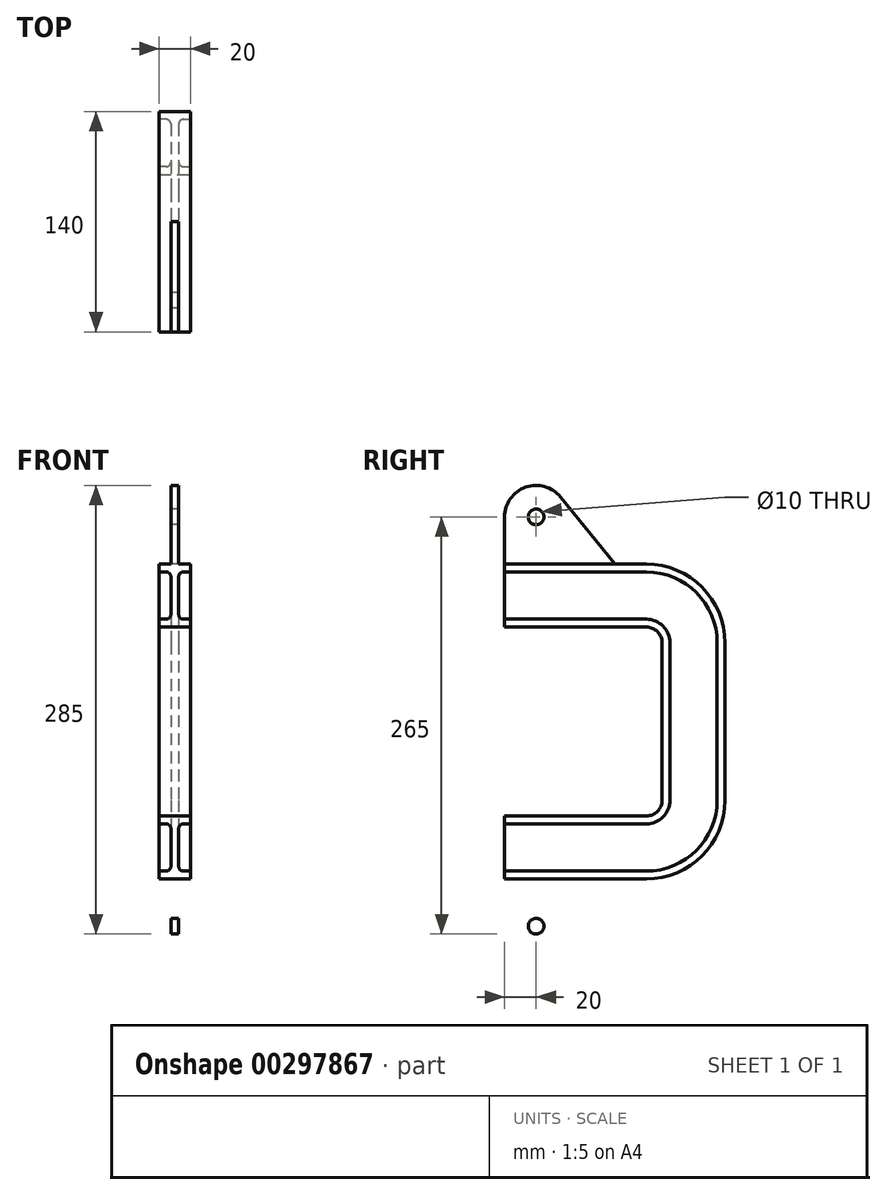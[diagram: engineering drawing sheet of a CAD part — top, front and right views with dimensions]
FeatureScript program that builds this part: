
annotation { "Feature Type Name" : "Feature", "Feature Type Description" : "" }
export const myFeature = defineFeature(function(context is Context, id is Id, definition is map)
    precondition{}
    {
        {
            var Q0;
            Q0=qCreatedBy(makeId("Front.planeOp"),FACE);
            var sketch = newSketch(context, id + "F0", { "sketchPlane" : qUnion([Q0])});
            skLineSegment(sketch, "E0", {"start": v(2.5, 0) * mm, "end": v(2.5, 12) * mm});
            skLineSegment(sketch, "E1", {"start": v(5.5, 15) * mm, "end": v(10, 15) * mm});
            skLineSegment(sketch, "E2", {"start": v(10, 15) * mm, "end": v(10, 20) * mm});
            skLineSegment(sketch, "E3", {"start": v(10, 20) * mm, "end": v(0, 20) * mm});
            skLineSegment(sketch, "E4.MirrorCS", {"start": v(-10, 15) * mm, "end": v(-10, 20) * mm});
            skLineSegment(sketch, "E5.MirrorCS", {"start": v(-5.5, 15) * mm, "end": v(-10, 15) * mm});
            skLineSegment(sketch, "E6.MirrorCS", {"start": v(-2.5, 0) * mm, "end": v(-2.5, 12) * mm});
            skLineSegment(sketch, "E7.MirrorCS", {"start": v(-10, 20) * mm, "end": v(0, 20) * mm});
            skLineSegment(sketch, "E8.MirrorCS", {"start": v(5.5, -15) * mm, "end": v(10, -15) * mm});
            skLineSegment(sketch, "E9.MirrorCS", {"start": v(-10, -15) * mm, "end": v(-10, -20) * mm});
            skLineSegment(sketch, "E10.MirrorCS", {"start": v(-5.5, -15) * mm, "end": v(-10, -15) * mm});
            skLineSegment(sketch, "E11.MirrorCS", {"start": v(10, -15) * mm, "end": v(10, -20) * mm});
            skLineSegment(sketch, "E12.MirrorCS", {"start": v(-10, -20) * mm, "end": v(0, -20) * mm});
            skLineSegment(sketch, "E13.MirrorCS", {"start": v(-2.5, 0) * mm, "end": v(-2.5, -12) * mm});
            skLineSegment(sketch, "E14.MirrorCS", {"start": v(10, -20) * mm, "end": v(0, -20) * mm});
            skLineSegment(sketch, "E15.MirrorCS", {"start": v(2.5, 0) * mm, "end": v(2.5, -12) * mm});
            skPoint(sketch, "E16.visualSharp", {"position": v(2.5, 15) * mm});
            skArc(sketch, "E16.filletArc", {"start": v(5.5, 15) * mm, "mid": v(3.38, 14.12) * mm, "end": v(2.5, 12) * mm});
            skPoint(sketch, "E17.visualSharp", {"position": v(-2.5, 15) * mm});
            skArc(sketch, "E17.filletArc", {"start": v(-2.5, 12) * mm, "mid": v(-3.38, 14.12) * mm, "end": v(-5.5, 15) * mm});
            skPoint(sketch, "E18.visualSharp", {"position": v(-2.5, -15) * mm});
            skArc(sketch, "E18.filletArc", {"start": v(-5.5, -15) * mm, "mid": v(-3.38, -14.12) * mm, "end": v(-2.5, -12) * mm});
            skPoint(sketch, "E19.visualSharp", {"position": v(2.5, -15) * mm});
            skArc(sketch, "E19.filletArc", {"start": v(2.5, -12) * mm, "mid": v(3.38, -14.12) * mm, "end": v(5.5, -15) * mm});
            skSolve(sketch);
        }
        {
            var Q0;
            Q0=qCreatedBy(makeId("Right.planeOp"),FACE);
            var sketch = newSketch(context, id + "F1", { "sketchPlane" : qUnion([Q0])});
            skLineSegment(sketch, "E20", {"start": v(0, -20) * mm, "end": v(90, -20) * mm});
            skLineSegment(sketch, "E21", {"start": v(100, -30) * mm, "end": v(100, -80) * mm});
            skPoint(sketch, "E22.visualSharp", {"position": v(100, -20) * mm});
            skArc(sketch, "E22.filletArc", {"start": v(100, -30) * mm, "mid": v(97.07, -22.93) * mm, "end": v(90, -20) * mm});
            skLineSegment(sketch, "E23", {"start": v(78.8, -80) * mm, "end": v(145.09, -80) * mm, "construction": true});
            skArc(sketch, "E24.MirrorCS", {"start": v(100, -130) * mm, "mid": v(97.07, -137.07) * mm, "end": v(90, -140) * mm});
            skLineSegment(sketch, "E25.MirrorCS", {"start": v(100, -130) * mm, "end": v(100, -80) * mm});
            skLineSegment(sketch, "E26.MirrorCS", {"start": v(0, -140) * mm, "end": v(90, -140) * mm});
            skPoint(sketch, "E27.MirrorP", {"position": v(100, -140) * mm});
            skSolve(sketch);
        }
        {
            var Q0;
            Q0=makeQuery(id+"F0.imprint","IMPRINT",FACE,{"disambiguationData":[TD([[makeQuery(id+"F0.imprint","IMPRINT",EDGE,{"derivedFrom":sQuery(id+"F0.wireOp",EDGE,"E0")}),1.0]])]});
            var Q1;
            Q1 = qSketchRegion(id + "F3", true);
            var Q2;
            Q2=sQuery(id+"F1.wireOp",EDGE,"E20");
            var Q3;
            Q3=sQuery(id+"F1.wireOp",EDGE,"E21");
            var Q4;
            Q4=sQuery(id+"F1.wireOp",EDGE,"E22.filletArc");
            var Q5;
            Q5=sQuery(id+"F1.wireOp",EDGE,"E25.MirrorCS");
            var Q6;
            Q6=sQuery(id+"F1.wireOp",EDGE,"E24.MirrorCS");
            var Q7;
            Q7=sQuery(id+"F1.wireOp",EDGE,"E26.MirrorCS");
            sweep(context, id + "F2", {"profiles" : qUnion([Q0, Q1]), "path" : qUnion([Q2, Q3, Q4, Q5, Q6, Q7])});
        }
        {
            var Q0;
            Q0=qCreatedBy(makeId("Right.planeOp"),FACE);
            var sketch = newSketch(context, id + "F3", { "sketchPlane" : qUnion([Q0])});
            skLineSegment(sketch, "E28", {"start": v(0, 20) * mm, "end": v(70, 20) * mm});
            skLineSegment(sketch, "E29", {"start": v(70, 20) * mm, "end": v(35.55, 62.58) * mm});
            skArc(sketch, "E30", {"start": v(35.55, 62.58) * mm, "mid": v(13.33, 68.85) * mm, "end": v(0, 50) * mm});
            skLineSegment(sketch, "E31", {"start": v(0, 20) * mm, "end": v(0, 50) * mm});
            skCircle(sketch, "E32", {"center": v(20, 50) * mm, "radius": 5 * mm});
            skLineSegment(sketch, "E33", {"start": v(26.9, -80) * mm, "end": v(176.51, -80) * mm, "construction": true});
            skCircle(sketch, "E34.MirrorC", {"center": v(20, -210) * mm, "radius": 5 * mm});
            skLineSegment(sketch, "E35.MirrorCS", {"start": v(0, -180) * mm, "end": v(0, -210) * mm});
            skArc(sketch, "E36.MirrorCS", {"start": v(35.55, -222.58) * mm, "mid": v(13.33, -228.85) * mm, "end": v(0, -210) * mm});
            skLineSegment(sketch, "E37.MirrorCS", {"start": v(0, -180) * mm, "end": v(70, -180) * mm});
            skLineSegment(sketch, "E38.MirrorCS", {"start": v(70, -180) * mm, "end": v(35.55, -222.58) * mm});
            skSolve(sketch);
        }
        {
            var Q0;
            Q0=makeQuery(id+"F3.imprint","IMPRINT",FACE,{"disambiguationData":[TD([[makeQuery(id+"F3.imprint","IMPRINT",EDGE,{"derivedFrom":sQuery(id+"F3.wireOp",EDGE,"E28")}),1.0]])]});
            var Q1;
            Q1=makeQuery(id+"F3.imprint","IMPRINT",FACE,{"disambiguationData":[TD([[makeQuery(id+"F3.imprint","IMPRINT",EDGE,{"derivedFrom":sQuery(id+"F3.wireOp",EDGE,"E34.MirrorC")}),1.0]])]});
            extrude(context, id + "F4", {"entities" : qUnion([Q0, Q1]), "operationType" : NewBodyOperationType.ADD, "endBound" : BoundingType.SYMMETRIC, "depth" : 5 * mm});
        }
    });
